# Revit family: Console Lavatory_TOTO_PJS06
name_source: partatom
category: 衛生器具
revit_build: Autodesk Revit 2018 (Build: 20170223_1515(x64)
units: mm (PartAtom-declared; Revit-internal decimal feet)

## family parameters
OmniClass タイトル = Sanitary, Laundry, and Cleaning Equipment
OmniClass 番号 = 23.45.00.00
パーツ タイプ = 標準
ロード時にボイドで切り取り = いいえ
丸型コネクタ寸法 = 直径を使用
作業面ベース = いいえ
共有 = いいえ
常に垂直 = はい
部屋計算ポイント = いいえ

## types (1)
- Console Lavatory_TOTO_PJS06
    Finish = basin_material
    Height = 180  [stored 0.590551 ft]
    Length = 380
    TOTO AsiaOceania = PJS06WE
    TOTO China = PJS06
    TOTO Europe = PJS06WEE
    TOTO HongKong = PJS06WE
    TOTO India = PJS06WE
    TOTO Korea = PJS06WE
    TOTO Taiwan = PJS06WET
    TOTO Thailand = PJS06WE
    TOTO Vietnam = PJS06WE
    Width = 600  [stored 1.9685 ft]
    排気配管 = いいえ
    排水配管 = いいえ
    水配管 = いいえ
    温水配管 = いいえ
    製造元 = TOTO Ltd.
    説明 = Console Lavatory/桌上式洗脸盆

note: [stored X ft] marks values corroborated as IEEE doubles in the binary element streams (Revit-internal decimal feet)

## geometry (parser evidence)
native form markers: Sweep x2
no freeform markers — native parametric forms only
